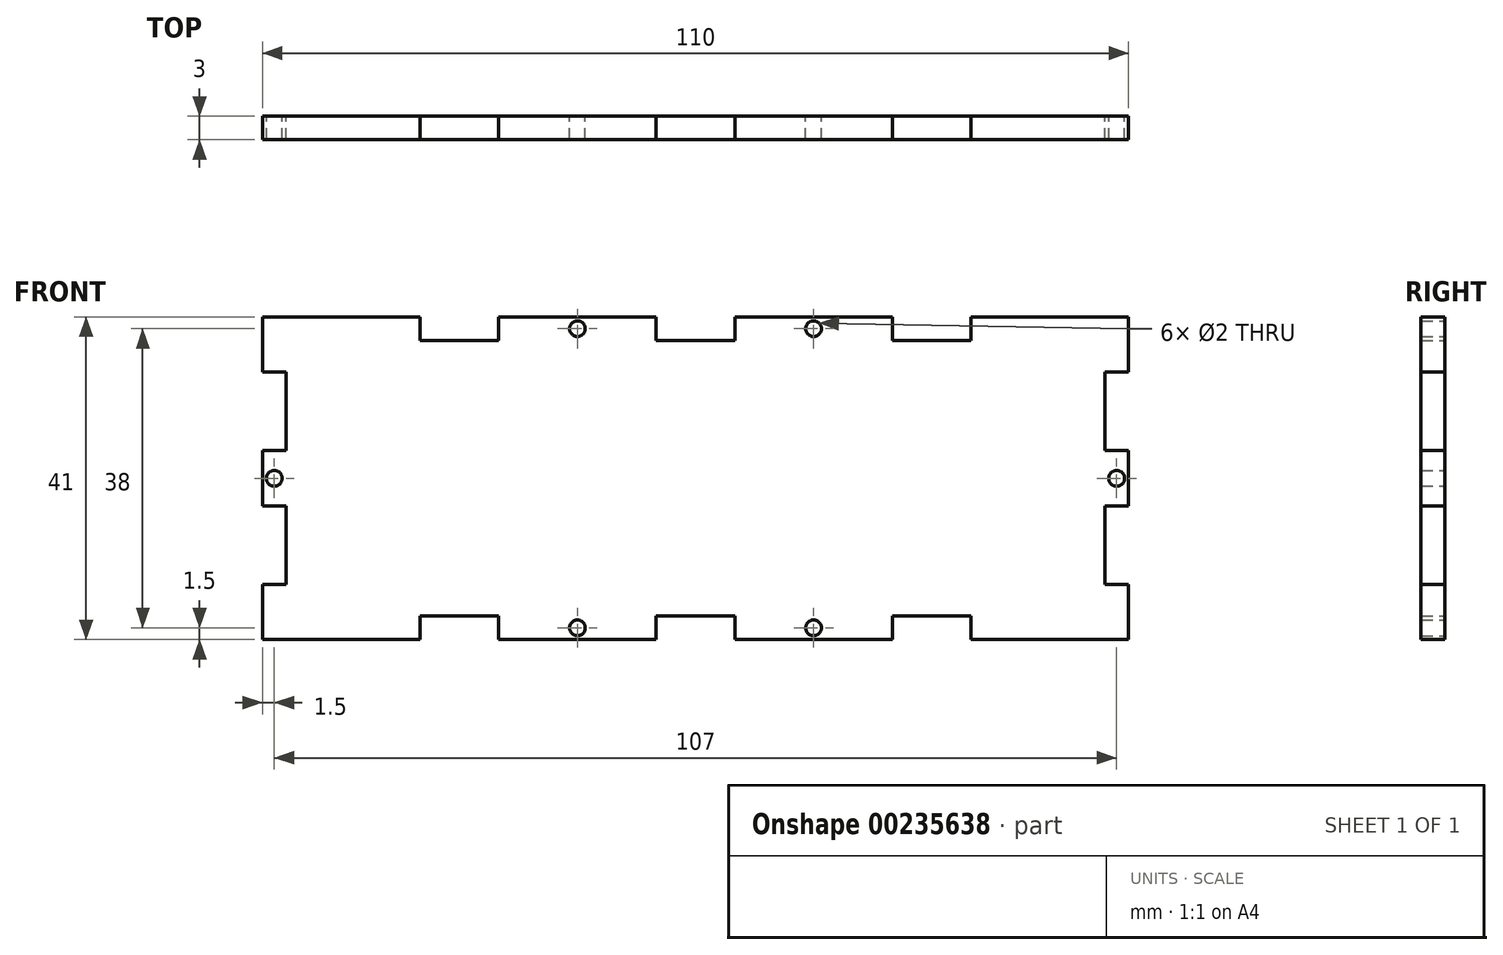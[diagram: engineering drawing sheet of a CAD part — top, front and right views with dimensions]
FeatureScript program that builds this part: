
annotation { "Feature Type Name" : "Feature", "Feature Type Description" : "" }
export const myFeature = defineFeature(function(context is Context, id is Id, definition is map)
    precondition{}
    {
        {
            var Q0;
            Q0=qCreatedBy(makeId("Front.planeOp"),FACE);
            var sketch = newSketch(context, id + "F0", { "sketchPlane" : qUnion([Q0])});
            skLineSegment(sketch, "E0", {"start": v(0, 0) * mm, "end": v(0, 7) * mm});
            skLineSegment(sketch, "E1", {"start": v(0, 7) * mm, "end": v(-3, 7) * mm});
            skLineSegment(sketch, "E2", {"start": v(-3, 7) * mm, "end": v(-3, 17) * mm});
            skLineSegment(sketch, "E3", {"start": v(-3, 17) * mm, "end": v(0, 17) * mm});
            skLineSegment(sketch, "E4", {"start": v(0, 17) * mm, "end": v(0, 24) * mm});
            skLineSegment(sketch, "E5", {"start": v(0, 24) * mm, "end": v(-3, 24) * mm});
            skLineSegment(sketch, "E6", {"start": v(-3, 24) * mm, "end": v(-3, 34) * mm});
            skLineSegment(sketch, "E7", {"start": v(-3, 34) * mm, "end": v(0, 34) * mm});
            skLineSegment(sketch, "E8", {"start": v(0, 34) * mm, "end": v(0, 41) * mm});
            skLineSegment(sketch, "E9", {"start": v(0, 41) * mm, "end": v(-20, 41) * mm});
            skLineSegment(sketch, "E10", {"start": v(-20, 41) * mm, "end": v(-20, 38) * mm});
            skLineSegment(sketch, "E11", {"start": v(-20, 38) * mm, "end": v(-30, 38) * mm});
            skLineSegment(sketch, "E12", {"start": v(-30, 38) * mm, "end": v(-30, 41) * mm});
            skLineSegment(sketch, "E13", {"start": v(-30, 41) * mm, "end": v(-50, 41) * mm});
            skLineSegment(sketch, "E14", {"start": v(-50, 41) * mm, "end": v(-50, 38) * mm});
            skLineSegment(sketch, "E15", {"start": v(-50, 38) * mm, "end": v(-55, 38) * mm});
            skLineSegment(sketch, "E16", {"start": v(0, 0) * mm, "end": v(-20, 0) * mm});
            skLineSegment(sketch, "E17", {"start": v(-20, 0) * mm, "end": v(-20, 3) * mm});
            skLineSegment(sketch, "E18", {"start": v(-20, 3) * mm, "end": v(-30, 3) * mm});
            skLineSegment(sketch, "E19", {"start": v(-30, 3) * mm, "end": v(-30, 0) * mm});
            skLineSegment(sketch, "E20", {"start": v(-30, 0) * mm, "end": v(-50, 0) * mm});
            skLineSegment(sketch, "E21", {"start": v(-50, 3) * mm, "end": v(-55, 3) * mm});
            skLineSegment(sketch, "E22", {"start": v(-50, 3) * mm, "end": v(-50, 0) * mm});
            skLineSegment(sketch, "E23", {"start": v(-55, 38) * mm, "end": v(-55, 3) * mm, "construction": true});
            skLineSegment(sketch, "E24.MirrorCS", {"start": v(-60, 38) * mm, "end": v(-55, 38) * mm});
            skLineSegment(sketch, "E25.MirrorCS", {"start": v(-60, 3) * mm, "end": v(-55, 3) * mm});
            skLineSegment(sketch, "E26.MirrorCS", {"start": v(-60, 41) * mm, "end": v(-60, 38) * mm});
            skLineSegment(sketch, "E27.MirrorCS", {"start": v(-60, 3) * mm, "end": v(-60, 0) * mm});
            skLineSegment(sketch, "E28.MirrorCS", {"start": v(-80, 3) * mm, "end": v(-80, 0) * mm});
            skLineSegment(sketch, "E29.MirrorCS", {"start": v(-80, 38) * mm, "end": v(-80, 41) * mm});
            skLineSegment(sketch, "E30.MirrorCS", {"start": v(-110, 7) * mm, "end": v(-107, 7) * mm});
            skLineSegment(sketch, "E31.MirrorCS", {"start": v(-90, 0) * mm, "end": v(-90, 3) * mm});
            skLineSegment(sketch, "E32.MirrorCS", {"start": v(-107, 17) * mm, "end": v(-110, 17) * mm});
            skLineSegment(sketch, "E33.MirrorCS", {"start": v(-110, 24) * mm, "end": v(-107, 24) * mm});
            skLineSegment(sketch, "E34.MirrorCS", {"start": v(-107, 34) * mm, "end": v(-110, 34) * mm});
            skLineSegment(sketch, "E35.MirrorCS", {"start": v(-90, 41) * mm, "end": v(-90, 38) * mm});
            skLineSegment(sketch, "E36.MirrorCS", {"start": v(-80, 0) * mm, "end": v(-60, 0) * mm});
            skLineSegment(sketch, "E37.MirrorCS", {"start": v(-110, 0) * mm, "end": v(-90, 0) * mm});
            skLineSegment(sketch, "E38.MirrorCS", {"start": v(-110, 17) * mm, "end": v(-110, 24) * mm});
            skLineSegment(sketch, "E39.MirrorCS", {"start": v(-110, 0) * mm, "end": v(-110, 7) * mm});
            skLineSegment(sketch, "E40.MirrorCS", {"start": v(-80, 41) * mm, "end": v(-60, 41) * mm});
            skLineSegment(sketch, "E41.MirrorCS", {"start": v(-90, 3) * mm, "end": v(-80, 3) * mm});
            skLineSegment(sketch, "E42.MirrorCS", {"start": v(-110, 41) * mm, "end": v(-90, 41) * mm});
            skLineSegment(sketch, "E43.MirrorCS", {"start": v(-110, 34) * mm, "end": v(-110, 41) * mm});
            skLineSegment(sketch, "E44.MirrorCS", {"start": v(-107, 7) * mm, "end": v(-107, 17) * mm});
            skLineSegment(sketch, "E45.MirrorCS", {"start": v(-90, 38) * mm, "end": v(-80, 38) * mm});
            skLineSegment(sketch, "E46.MirrorCS", {"start": v(-107, 24) * mm, "end": v(-107, 34) * mm});
            skPoint(sketch, "E47.centerSnap0", {"position": v(-108.5, 24) * mm});
            skPoint(sketch, "E47.centerSnap1", {"position": v(-110, 20.5) * mm});
            skPoint(sketch, "E48.centerSnap0", {"position": v(-70, 0) * mm});
            skPoint(sketch, "E48.centerSnap1", {"position": v(-80, 1.5) * mm});
            skPoint(sketch, "E49.centerSnap0", {"position": v(-50, 1.5) * mm});
            skPoint(sketch, "E49.centerSnap1", {"position": v(-40, 0) * mm});
            skPoint(sketch, "E50.centerSnap0", {"position": v(-60, 39.5) * mm});
            skPoint(sketch, "E50.centerSnap1", {"position": v(-70, 41) * mm});
            skCircle(sketch, "E51", {"center": v(-70, 39.5) * mm, "radius": 1 * mm});
            skCircle(sketch, "E52", {"center": v(-1.5, 20.5) * mm, "radius": 1 * mm});
            skPoint(sketch, "E52.centerSnap0", {"position": v(0, 20.5) * mm});
            skPoint(sketch, "E52.centerSnap1", {"position": v(-1.5, 17) * mm});
            skPoint(sketch, "E53.centerSnap0", {"position": v(-50, 39.5) * mm});
            skPoint(sketch, "E53.centerSnap1", {"position": v(-40, 41) * mm});
            skCircle(sketch, "E54", {"center": v(-40, 39.5) * mm, "radius": 1 * mm});
            skPoint(sketch, "E54.centerSnap0", {"position": v(-30, 39.5) * mm});
            skCircle(sketch, "E55", {"center": v(-108.5, 20.5) * mm, "radius": 1 * mm});
            skCircle(sketch, "E56", {"center": v(-70, 1.5) * mm, "radius": 1 * mm});
            skCircle(sketch, "E57", {"center": v(-40, 1.5) * mm, "radius": 1 * mm});
            skSolve(sketch);
        }
        {
            var Q0;
            Q0=makeQuery(id+"F0.imprint","IMPRINT",FACE,{"disambiguationData":[TD([[makeQuery(id+"F0.imprint","IMPRINT",EDGE,{"derivedFrom":sQuery(id+"F0.wireOp",EDGE,"E0")}),1.0]])]});
            extrude(context, id + "F1", {"entities" : qUnion([Q0]), "depth" : 3 * mm});
        }
    });
